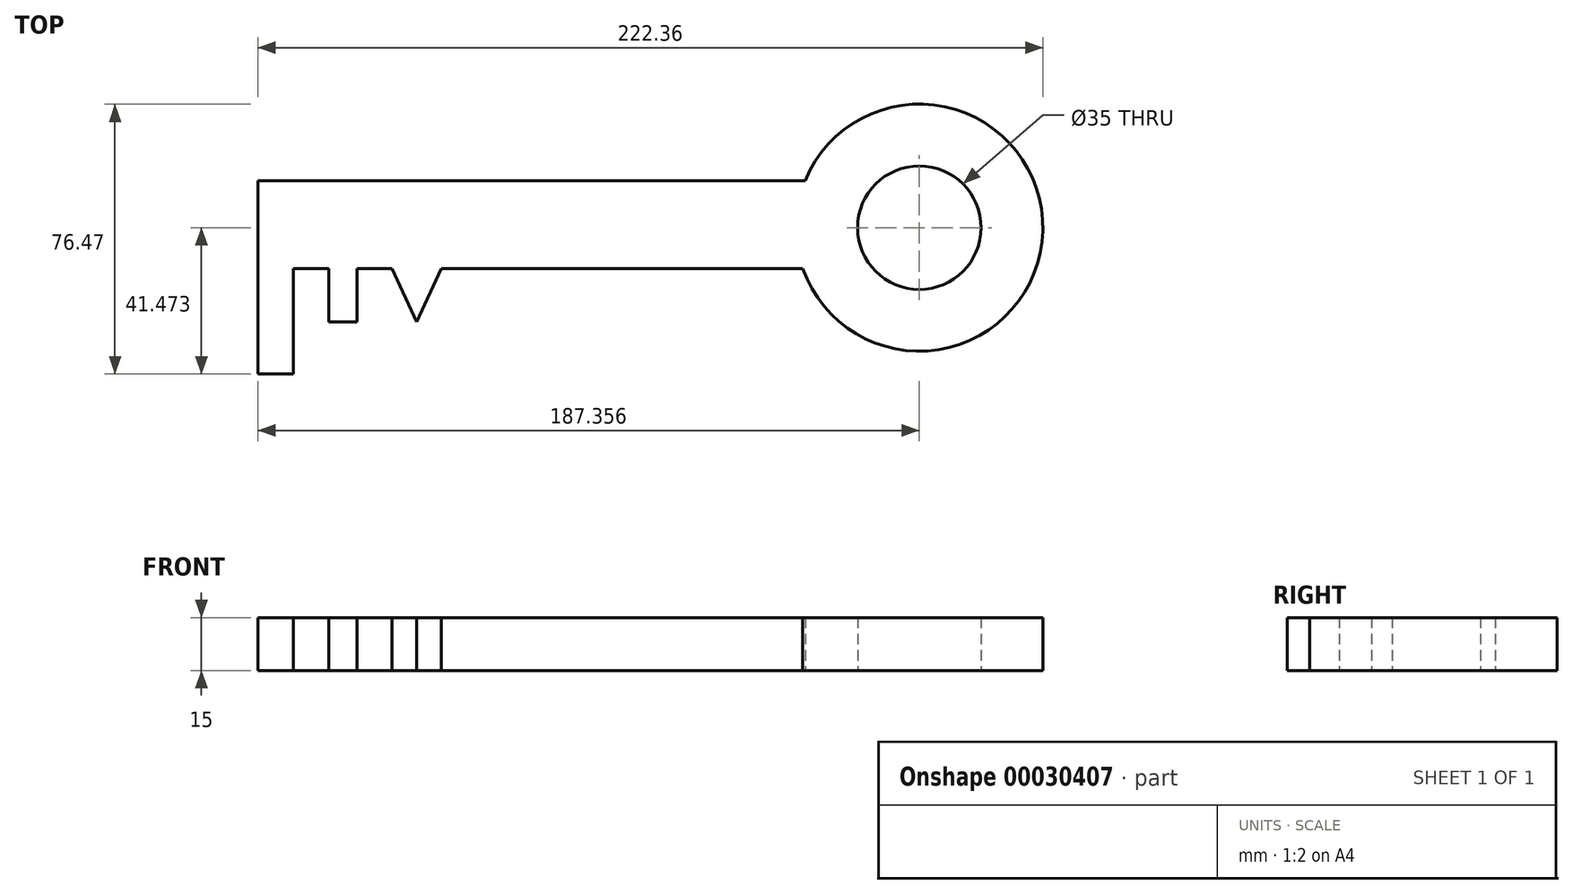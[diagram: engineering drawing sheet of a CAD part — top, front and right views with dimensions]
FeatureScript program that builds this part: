
annotation { "Feature Type Name" : "Feature", "Feature Type Description" : "" }
export const myFeature = defineFeature(function(context is Context, id is Id, definition is map)
    precondition{}
    {
        {
            var Q0;
            Q0=qCreatedBy(makeId("Top.planeOp"),FACE);
            var sketch = newSketch(context, id + "F0", { "sketchPlane" : qUnion([Q0])});
            skLineSegment(sketch, "E0.bottom", {"start": v(-61.49, 25) * mm, "end": v(93.51, 25) * mm});
            skLineSegment(sketch, "E0.top", {"start": v(-61.49, 0) * mm, "end": v(93.51, 0) * mm});
            skLineSegment(sketch, "E0.left", {"start": v(-61.49, 25) * mm, "end": v(-61.49, 0) * mm});
            skLineSegment(sketch, "E1.bottom", {"start": v(-61.49, 0.18) * mm, "end": v(-51.49, 0.18) * mm});
            skLineSegment(sketch, "E1.top", {"start": v(-61.49, -29.82) * mm, "end": v(-51.49, -29.82) * mm});
            skLineSegment(sketch, "E1.left", {"start": v(-61.49, 0.18) * mm, "end": v(-61.49, -29.82) * mm});
            skLineSegment(sketch, "E1.right", {"start": v(-51.49, 0.18) * mm, "end": v(-51.49, -29.82) * mm});
            skLineSegment(sketch, "E2.bottom", {"start": v(-41.49, 0) * mm, "end": v(-33.49, 0) * mm});
            skLineSegment(sketch, "E2.top", {"start": v(-41.49, -15) * mm, "end": v(-33.49, -15) * mm});
            skLineSegment(sketch, "E2.left", {"start": v(-41.49, 0) * mm, "end": v(-41.49, -15) * mm});
            skLineSegment(sketch, "E2.right", {"start": v(-33.49, 0) * mm, "end": v(-33.49, -15) * mm});
            skLineSegment(sketch, "E3", {"start": v(-23.49, 0) * mm, "end": v(-16.49, -15) * mm});
            skLineSegment(sketch, "E4", {"start": v(-16.49, -15) * mm, "end": v(-9.49, 0) * mm});
            skArc(sketch, "E5", {"start": v(92.86, 0) * mm, "mid": v(160.85, 10.75) * mm, "end": v(93.51, 25) * mm});
            skCircle(sketch, "E6", {"center": v(125.87, 11.65) * mm, "radius": 17.5 * mm});
            skLineSegment(sketch, "E7", {"start": v(-61.49, 12.5) * mm, "end": v(125.87, 11.65) * mm, "construction": true});
            skSolve(sketch);
        }
        {
            var Q0;
            Q0 = qSketchRegion(id + "F0", true);
            extrude(context, id + "F1", {"entities" : qUnion([Q0]), "depth" : 15 * mm});
        }
    });
